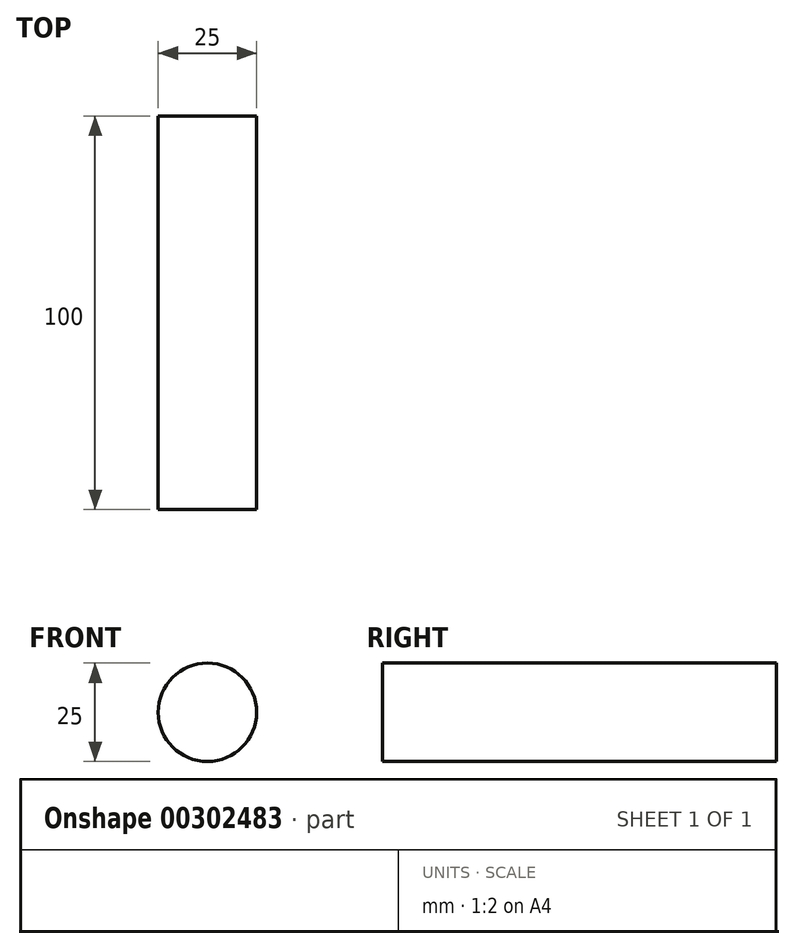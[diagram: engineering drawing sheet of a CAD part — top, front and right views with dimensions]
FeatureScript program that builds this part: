
annotation { "Feature Type Name" : "Feature", "Feature Type Description" : "" }
export const myFeature = defineFeature(function(context is Context, id is Id, definition is map)
    precondition{}
    {
        {
            var Q0;
            Q0=qCreatedBy(makeId("Front.planeOp"),FACE);
            var sketch = newSketch(context, id + "F0", { "sketchPlane" : qUnion([Q0])});
            skCircle(sketch, "E0", {"center": v(0, 100) * mm, "radius": 12.5 * mm});
            skSolve(sketch);
        }
        {
            var Q0;
            Q0=makeQuery(id+"F0.imprint","IMPRINT",FACE,{"disambiguationData":[TD([[makeQuery(id+"F0.imprint","IMPRINT",EDGE,{"derivedFrom":sQuery(id+"F0.wireOp",EDGE,"E0")}),1.0]])]});
            var Q1;
            Q1=sQuery(id+"F0.wireOp",EDGE,"E0");
            extrude(context, id + "F1", {"entities" : qUnion([Q0]), "surfaceEntities" : qUnion([Q1]), "oppositeDirection" : true, "depth" : 50 * mm, "hasSecondDirection" : true, "secondDirectionOppositeDirection" : false, "secondDirectionDepth" : 50 * mm});
        }
    });
